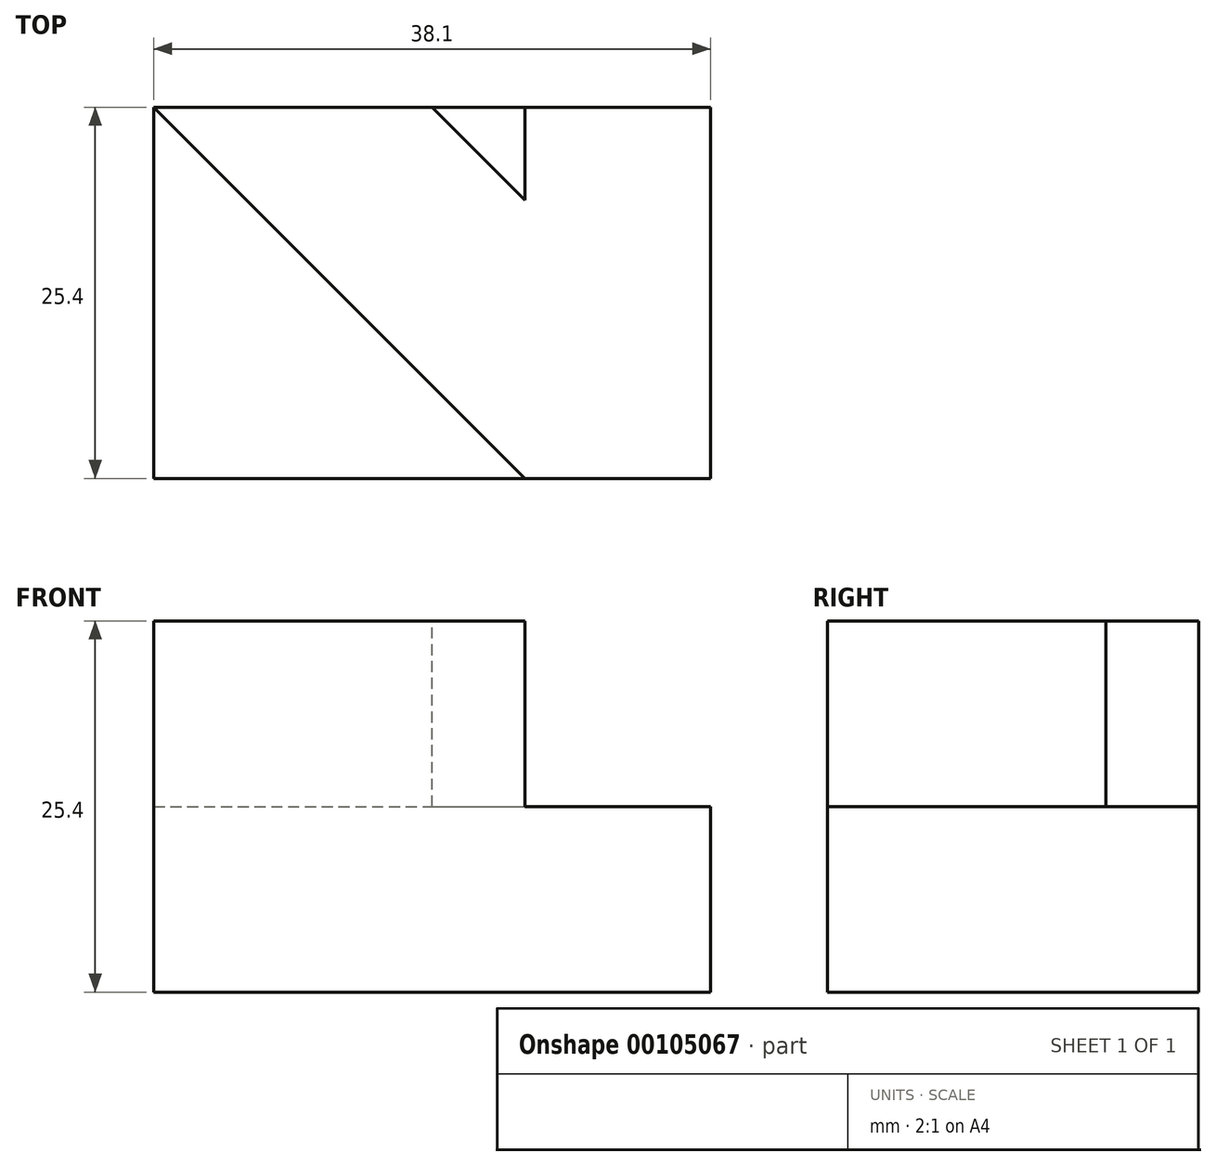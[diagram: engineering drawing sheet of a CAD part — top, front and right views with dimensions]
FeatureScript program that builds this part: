
annotation { "Feature Type Name" : "Feature", "Feature Type Description" : "" }
export const myFeature = defineFeature(function(context is Context, id is Id, definition is map)
    precondition{}
    {
        {
            var Q0;
            Q0=qCreatedBy(makeId("Front.planeOp"),FACE);
            var sketch = newSketch(context, id + "F0", { "sketchPlane" : qUnion([Q0])});
            skLineSegment(sketch, "E0.bottom", {"start": v(0, -25.4) * mm, "end": v(38.1, -25.4) * mm});
            skLineSegment(sketch, "E0.top", {"start": v(0, 0) * mm, "end": v(38.1, 0) * mm});
            skLineSegment(sketch, "E0.left", {"start": v(0, -25.4) * mm, "end": v(0, 0) * mm});
            skLineSegment(sketch, "E0.right", {"start": v(38.1, -25.4) * mm, "end": v(38.1, 0) * mm});
            skLineSegment(sketch, "E1.bottom", {"start": v(38.1, 0) * mm, "end": v(25.4, 0) * mm});
            skLineSegment(sketch, "E1.top", {"start": v(38.1, -12.7) * mm, "end": v(25.4, -12.7) * mm});
            skLineSegment(sketch, "E1.left", {"start": v(38.1, 0) * mm, "end": v(38.1, 0) * mm});
            skLineSegment(sketch, "E1.right", {"start": v(25.4, 0) * mm, "end": v(25.4, -12.7) * mm});
            skSolve(sketch);
        }
        {
            var Q0;
            Q0=qCreatedBy(makeId("Top.planeOp"),FACE);
            var sketch = newSketch(context, id + "F1", { "sketchPlane" : qUnion([Q0])});
            skLineSegment(sketch, "E2.bottom", {"start": v(0, 0) * mm, "end": v(38.1, 0) * mm});
            skLineSegment(sketch, "E2.top", {"start": v(0, 25.4) * mm, "end": v(38.1, 25.4) * mm});
            skLineSegment(sketch, "E2.left", {"start": v(0, 0) * mm, "end": v(0, 25.4) * mm});
            skLineSegment(sketch, "E2.right", {"start": v(38.1, 0) * mm, "end": v(38.1, 25.4) * mm});
            skLineSegment(sketch, "E3", {"start": v(0, 25.4) * mm, "end": v(25.4, 0) * mm});
            skLineSegment(sketch, "E4", {"start": v(19.05, 25.4) * mm, "end": v(38.1, 6.35) * mm});
            skSolve(sketch);
        }
        {
            var Q0;
            Q0=makeQuery(id+"F0.imprint","IMPRINT",FACE,{"disambiguationData":[TD([[makeQuery(id+"F0.imprint","IMPRINT",EDGE,{"derivedFrom":sQuery(id+"F0.wireOp",EDGE,"E0.bottom")}),1.0]])]});
            var Q1;
            Q1=makeQuery(id+"F0.imprint","IMPRINT",FACE,{"disambiguationData":[TD([[makeQuery(id+"F0.imprint","IMPRINT",EDGE,{"derivedFrom":sQuery(id+"F0.wireOp",EDGE,"E1.bottom")}),1.0]])]});
            extrude(context, id + "F2", {"entities" : qUnion([Q0, Q1]), "oppositeDirection" : true, "depth" : 25.4 * mm});
        }
        {
            var Q0;
            {var subQ0=sQuery(id+"F1.wireOp",EDGE,"E3");Q0=makeQuery(id+"F1.imprint","IMPRINT",FACE,{"disambiguationData":[TD([[makeQuery(id+"F1.imprint","IMPRINT",EDGE,{"derivedFrom":subQ0}),1.0]])]});}
            extrude(context, id + "F3", {"entities" : qUnion([Q0]), "operationType" : NewBodyOperationType.REMOVE, "oppositeDirection" : true, "depth" : 12.7 * mm});
        }
    });
